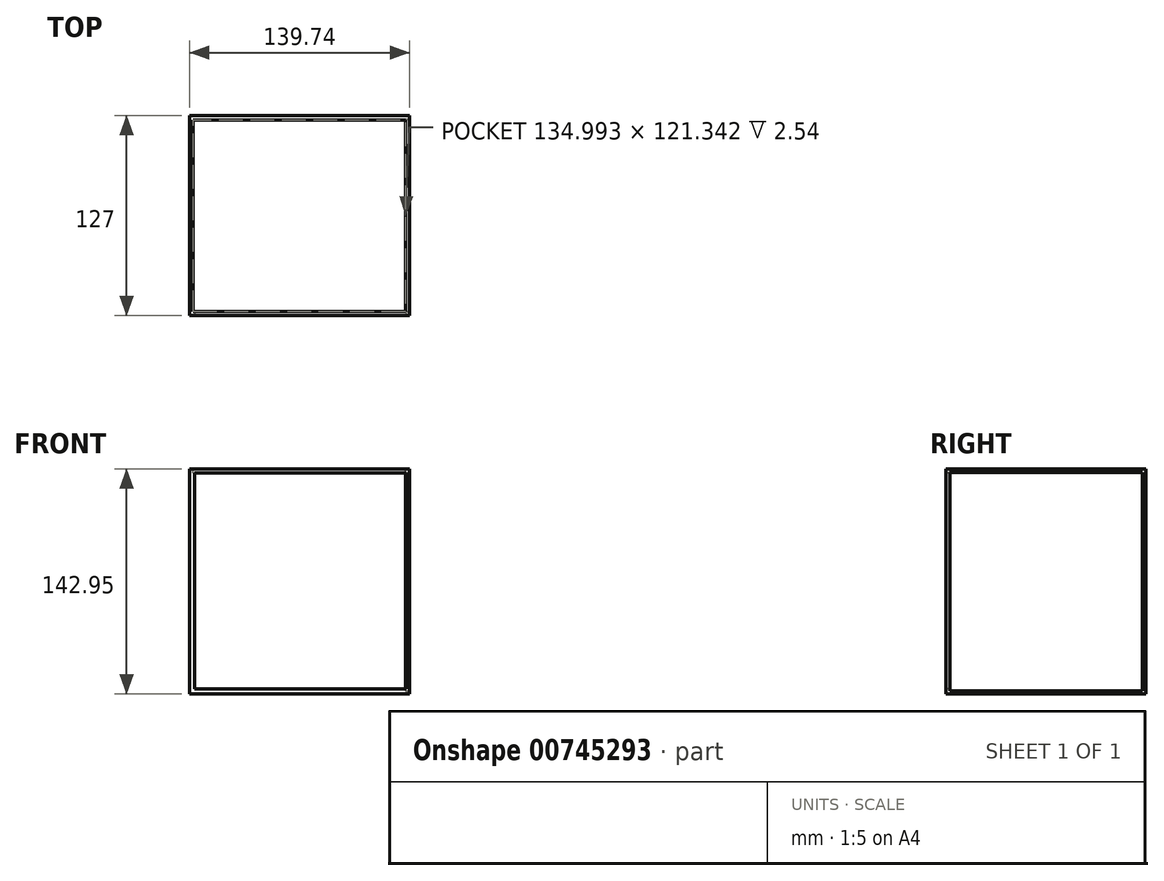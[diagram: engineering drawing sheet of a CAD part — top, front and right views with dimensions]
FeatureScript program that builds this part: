
annotation { "Feature Type Name" : "Feature", "Feature Type Description" : "" }
export const myFeature = defineFeature(function(context is Context, id is Id, definition is map)
    precondition{}
    {
        {
            var Q0;
            Q0=qCreatedBy(makeId("Front.planeOp"),FACE);
            var sketch = newSketch(context, id + "F0", { "sketchPlane" : qUnion([Q0])});
            skLineSegment(sketch, "E0.bottom", {"start": v(-69.49, 71.2) * mm, "end": v(70.25, 71.2) * mm});
            skLineSegment(sketch, "E0.top", {"start": v(-69.49, -71.76) * mm, "end": v(70.25, -71.76) * mm});
            skLineSegment(sketch, "E0.left", {"start": v(-69.49, 71.2) * mm, "end": v(-69.49, -71.76) * mm});
            skLineSegment(sketch, "E0.right", {"start": v(70.25, 71.2) * mm, "end": v(70.25, -71.76) * mm});
            skSolve(sketch);
        }
        {
            var Q0;
            Q0 = qSketchRegion(id + "F0", true);
            extrude(context, id + "F1", {"entities" : qUnion([Q0]), "depth" : 127 * mm, "offsetDistance" : 25.4 * mm});
        }
        {
            var Q0;
            Q0=makeQuery(id+"F1.opExtrude","SWEPT_FACE",FACE,{"disambiguationData":[OSD([sQuery(id+"F0.wireOp",EDGE,"E0.right")])]});
            var sketch = newSketch(context, id + "F2", { "sketchPlane" : qUnion([Q0])});
            skLineSegment(sketch, "E1.bottom", {"start": v(-124.46, 69.1) * mm, "end": v(-2.17, 69.1) * mm});
            skLineSegment(sketch, "E1.top", {"start": v(-124.46, -69.87) * mm, "end": v(-2.17, -69.87) * mm});
            skLineSegment(sketch, "E1.left", {"start": v(-124.46, 69.1) * mm, "end": v(-124.46, -69.87) * mm});
            skLineSegment(sketch, "E1.right", {"start": v(-2.17, 69.1) * mm, "end": v(-2.17, -69.87) * mm});
            skSolve(sketch);
        }
        {
            var Q0;
            Q0 = qSketchRegion(id + "F2", true);
            extrude(context, id + "F3", {"entities" : qUnion([Q0]), "operationType" : NewBodyOperationType.REMOVE, "oppositeDirection" : true, "depth" : 2.54 * mm, "offsetDistance" : 25.4 * mm});
        }
        {
            var Q0;
            Q0=makeQuery(id+"F1.opExtrude","CAP_FACE",FACE,{"disambiguationData":[OSD([sQuery(id+"F0.wireOp",EDGE,"E0.bottom"),sQuery(id+"F0.wireOp",EDGE,"E0.top"),sQuery(id+"F0.wireOp",EDGE,"E0.left"),sQuery(id+"F0.wireOp",EDGE,"E0.right")])],"isStart":false});
            var sketch = newSketch(context, id + "F4", { "sketchPlane" : qUnion([Q0])});
            skLineSegment(sketch, "E2.bottom", {"start": v(-66.45, 68.73) * mm, "end": v(67.97, 68.73) * mm});
            skLineSegment(sketch, "E2.top", {"start": v(-66.45, -68.54) * mm, "end": v(67.97, -68.54) * mm});
            skLineSegment(sketch, "E2.left", {"start": v(-66.45, 68.73) * mm, "end": v(-66.45, -68.54) * mm});
            skLineSegment(sketch, "E2.right", {"start": v(67.97, 68.73) * mm, "end": v(67.97, -68.54) * mm});
            skSolve(sketch);
        }
        {
            var Q0;
            Q0 = qSketchRegion(id + "F4", true);
            extrude(context, id + "F5", {"entities" : qUnion([Q0]), "operationType" : NewBodyOperationType.REMOVE, "oppositeDirection" : true, "depth" : 2.54 * mm, "offsetDistance" : 25.4 * mm});
        }
        {
            var Q0;
            Q0=makeQuery(id+"F1.opExtrude","SWEPT_FACE",FACE,{"disambiguationData":[OSD([sQuery(id+"F0.wireOp",EDGE,"E0.bottom")])]});
            var sketch = newSketch(context, id + "F6", { "sketchPlane" : qUnion([Q0])});
            skLineSegment(sketch, "E3.bottom", {"start": v(-67.37, -3.03) * mm, "end": v(67.62, -3.03) * mm});
            skLineSegment(sketch, "E3.top", {"start": v(-67.37, -124.37) * mm, "end": v(67.62, -124.37) * mm});
            skLineSegment(sketch, "E3.left", {"start": v(-67.37, -3.03) * mm, "end": v(-67.37, -124.37) * mm});
            skLineSegment(sketch, "E3.right", {"start": v(67.62, -3.03) * mm, "end": v(67.62, -124.37) * mm});
            skSolve(sketch);
        }
        {
            var Q0;
            Q0 = qSketchRegion(id + "F6", true);
            extrude(context, id + "F7", {"entities" : qUnion([Q0]), "operationType" : NewBodyOperationType.REMOVE, "oppositeDirection" : true, "depth" : 2.54 * mm, "offsetDistance" : 25.4 * mm});
        }
    });
